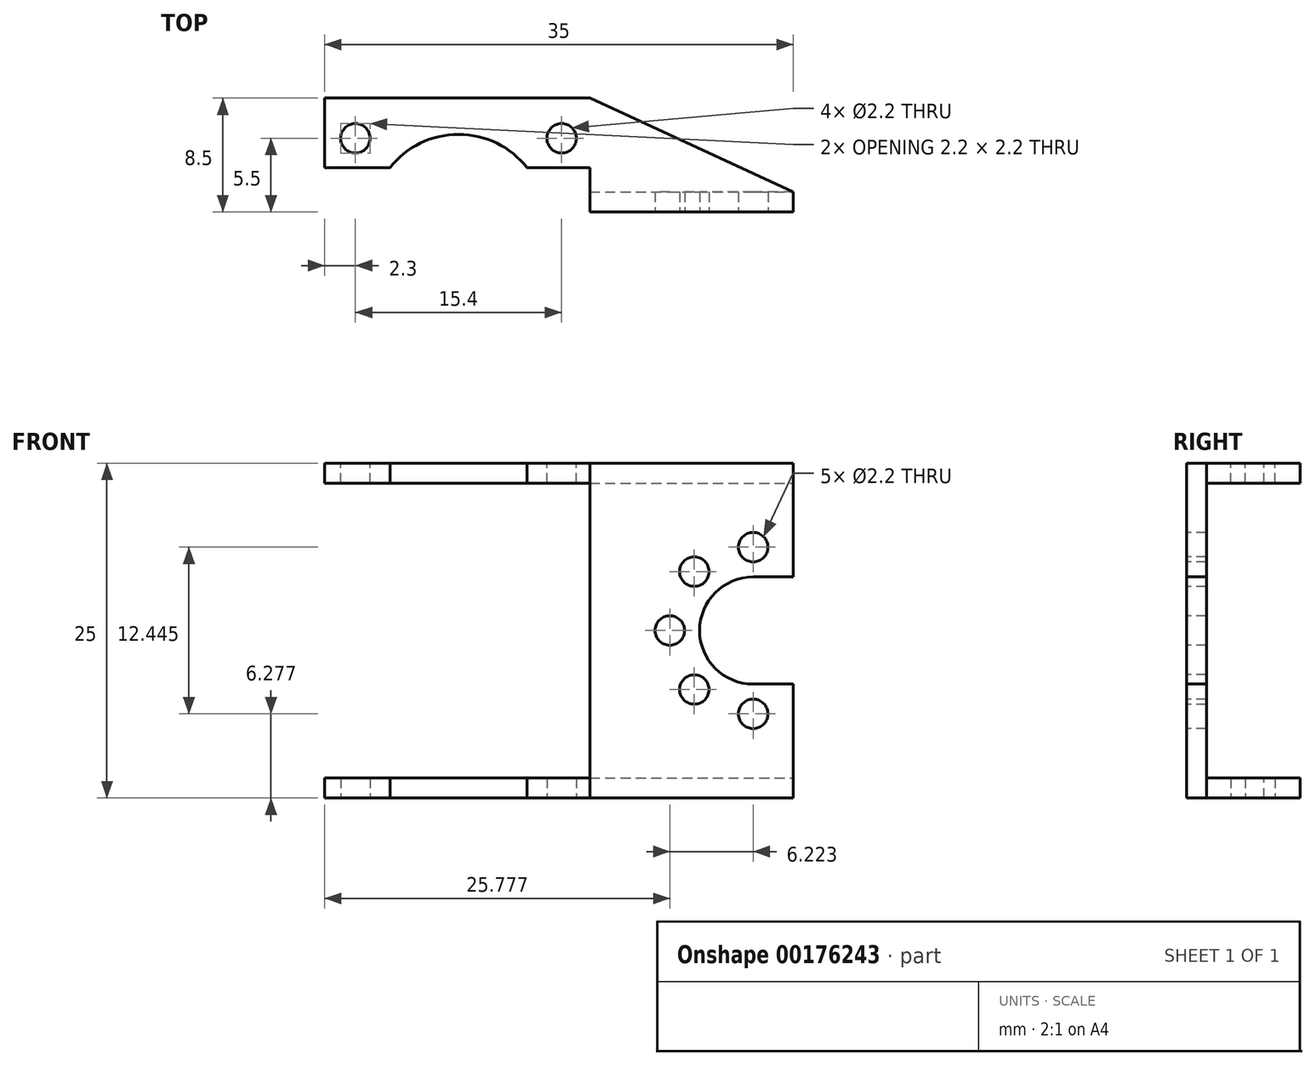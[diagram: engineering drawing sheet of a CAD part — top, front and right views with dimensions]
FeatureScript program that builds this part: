
annotation { "Feature Type Name" : "Feature", "Feature Type Description" : "" }
export const myFeature = defineFeature(function(context is Context, id is Id, definition is map)
    precondition{}
    {
        {
            var Q0;
            Q0=qCreatedBy(makeId("Top.planeOp"),FACE);
            var sketch = newSketch(context, id + "F0", { "sketchPlane" : qUnion([Q0])});
            skLineSegment(sketch, "E0.bottom", {"start": v(-10, 0.75) * mm, "end": v(10, 0.75) * mm});
            skLineSegment(sketch, "E0.top", {"start": v(-10, -0.75) * mm, "end": v(10, -0.75) * mm});
            skLineSegment(sketch, "E0.left", {"start": v(-10, 0.75) * mm, "end": v(-10, -0.75) * mm});
            skLineSegment(sketch, "E0.right", {"start": v(10, 0.75) * mm, "end": v(10, -0.75) * mm});
            skPoint(sketch, "E0.middle", {"position": v(0, 0) * mm});
            skSolve(sketch);
        }
        {
            var Q0;
            Q0=qSketchRegion(id+"F0",true);
            extrude(context, id + "F1", {"entities" : qUnion([Q0]), "depth" : (11 + 1.5) * mm});
        }
        {
            var Q0;
            Q0=makeQuery(id+"F1.opExtrude","SWEPT_FACE",FACE,{"disambiguationData":[OSD([sQuery(id+"F0.wireOp",EDGE,"E0.bottom")])]});
            var sketch = newSketch(context, id + "F2", { "sketchPlane" : qUnion([Q0])});
            skLineSegment(sketch, "E1.bottom", {"start": v(10, 12.5) * mm, "end": v(-10, 12.5) * mm});
            skLineSegment(sketch, "E1.top", {"start": v(10, 11) * mm, "end": v(-10, 11) * mm});
            skLineSegment(sketch, "E1.left", {"start": v(10, 12.5) * mm, "end": v(10, 11) * mm});
            skLineSegment(sketch, "E1.right", {"start": v(-10, 12.5) * mm, "end": v(-10, 11) * mm});
            skSolve(sketch);
        }
        {
            var Q0;
            Q0=qSketchRegion(id+"F2",true);
            extrude(context, id + "F3", {"entities" : qUnion([Q0]), "operationType" : NewBodyOperationType.ADD, "depth" : (10 - 1.5) * mm});
        }
        {
            var Q0;
            Q0=makeQuery(id+"F3.boolean.opBoolean","MERGE",FACE,{"derivedFrom":[makeQuery(id+"F1.opExtrude","CAP_FACE",FACE,{"disambiguationData":[OSD([sQuery(id+"F0.wireOp",EDGE,"E0.bottom"),sQuery(id+"F0.wireOp",EDGE,"E0.top"),sQuery(id+"F0.wireOp",EDGE,"E0.left"),sQuery(id+"F0.wireOp",EDGE,"E0.right")])],"isStart":false}),makeQuery(id+"F3.opExtrude","SWEPT_FACE",FACE,{"disambiguationData":[OSD([sQuery(id+"F2.wireOp",EDGE,"E1.bottom")])]})]});
            var sketch = newSketch(context, id + "F4", { "sketchPlane" : qUnion([Q0])});
            skLineSegment(sketch, "E2", {"start": v(-10, 4.75) * mm, "end": v(10, 4.75) * mm, "construction": true});
            skCircle(sketch, "E3", {"center": v(-7.7, 4.75) * mm, "radius": 1.1 * mm});
            skCircle(sketch, "E4.MirrorC", {"center": v(7.7, 4.75) * mm, "radius": 1.1 * mm});
            skSolve(sketch);
        }
        {
            var Q0;
            Q0=qSketchRegion(id+"F4",true);
            extrude(context, id + "F5", {"entities" : qUnion([Q0]), "operationType" : NewBodyOperationType.REMOVE, "endBound" : BoundingType.UP_TO_NEXT, "oppositeDirection" : true, "depth" : 25 * mm});
        }
        {
            var Q0;
            Q0=makeQuery(id+"F1.opExtrude","SWEPT_BODY",BODY,{"disambiguationData":[OSD([sQuery(id+"F0.wireOp",EDGE,"E0.bottom"),sQuery(id+"F0.wireOp",EDGE,"E0.top"),sQuery(id+"F0.wireOp",EDGE,"E0.left"),sQuery(id+"F0.wireOp",EDGE,"E0.right")])]});
            var Q1;
            Q1=qCreatedBy(makeId("Top.planeOp"),FACE);
            mirror(context, id + "F6", {"operationType" : NewBodyOperationType.ADD, "entities" : qUnion([Q0]), "mirrorPlane" : qUnion([Q1])});
        }
        {
            var Q0;
            {var subQ0=makeQuery(id+"F3.boolean.opBoolean","MERGE",FACE,{"derivedFrom":[makeQuery(id+"F1.opExtrude","SWEPT_FACE",FACE,{"disambiguationData":[OSD([sQuery(id+"F0.wireOp",EDGE,"E0.right")])]}),makeQuery(id+"F3.opExtrude","SWEPT_FACE",FACE,{"disambiguationData":[OSD([sQuery(id+"F2.wireOp",EDGE,"E1.right")])]})]});Q0=makeQuery(id+"F6.boolean.opBoolean","MERGE",FACE,{"derivedFrom":[subQ0,makeQuery(id+"F6.opPattern","COPY",FACE,{"derivedFrom":subQ0,"instanceName":"1"})]});}
            var sketch = newSketch(context, id + "F7", { "sketchPlane" : qUnion([Q0])});
            skLineSegment(sketch, "E5.0", {"start": v(9.25, -12.5) * mm, "end": v(-0.75, -12.5) * mm});
            skLineSegment(sketch, "E5.1", {"start": v(9.25, 11) * mm, "end": v(0.75, 11) * mm});
            skLineSegment(sketch, "E5.2", {"start": v(9.25, -11) * mm, "end": v(0.75, -11) * mm});
            skLineSegment(sketch, "E5.3", {"start": v(9.25, 12.5) * mm, "end": v(-0.75, 12.5) * mm});
            skLineSegment(sketch, "E5.4", {"start": v(9.25, 11) * mm, "end": v(0.75, 11) * mm});
            skLineSegment(sketch, "E5.5", {"start": v(5.85, 12.5) * mm, "end": v(3.65, 12.5) * mm});
            skLineSegment(sketch, "E5.7", {"start": v(9.25, -12.5) * mm, "end": v(-0.75, -12.5) * mm});
            skLineSegment(sketch, "E5.8", {"start": v(9.25, -12.5) * mm, "end": v(9.25, -11) * mm});
            skLineSegment(sketch, "E5.9", {"start": v(9.25, 12.5) * mm, "end": v(9.25, 11) * mm});
            skLineSegment(sketch, "E5.10", {"start": v(9.25, 12.5) * mm, "end": v(-0.75, 12.5) * mm});
            skLineSegment(sketch, "E5.13", {"start": v(9.25, -11) * mm, "end": v(0.75, -11) * mm});
            skLineSegment(sketch, "E5.14", {"start": v(0.75, 11) * mm, "end": v(0.75, -11) * mm});
            skLineSegment(sketch, "E5.15", {"start": v(-0.75, 12.5) * mm, "end": v(-0.75, -12.5) * mm});
            skLineSegment(sketch, "E5.16", {"start": v(5.85, -11) * mm, "end": v(3.65, -11) * mm});
            skLineSegment(sketch, "E5.20", {"start": v(5.85, 11) * mm, "end": v(3.65, 11) * mm});
            skLineSegment(sketch, "E5.21", {"start": v(3.65, -11) * mm, "end": v(5.85, -11) * mm});
            skLineSegment(sketch, "E5.22", {"start": v(-0.75, 12.5) * mm, "end": v(-0.75, -12.5) * mm});
            skLineSegment(sketch, "E5.23", {"start": v(5.85, -12.5) * mm, "end": v(3.65, -12.5) * mm});
            skLineSegment(sketch, "E5.24", {"start": v(0.75, 11) * mm, "end": v(0.75, -11) * mm});
            skLineSegment(sketch, "E5.26", {"start": v(3.65, 12.5) * mm, "end": v(5.85, 12.5) * mm});
            skLineSegment(sketch, "E5.28", {"start": v(9.25, -12.5) * mm, "end": v(9.25, -11) * mm});
            skLineSegment(sketch, "E5.29", {"start": v(3.65, -12.5) * mm, "end": v(5.85, -12.5) * mm});
            skLineSegment(sketch, "E5.30", {"start": v(9.25, 12.5) * mm, "end": v(9.25, 11) * mm});
            skLineSegment(sketch, "E5.31", {"start": v(3.65, 11) * mm, "end": v(5.85, 11) * mm});
            skSolve(sketch);
        }
        {
            var Q0;
            Q0=qSketchRegion(id+"F7",true);
            extrude(context, id + "F8", {"entities" : qUnion([Q0]), "operationType" : NewBodyOperationType.ADD, "depth" : 15 * mm});
        }
        {
            var Q0;
            {var subQ0=makeQuery(id+"F1.opExtrude","SWEPT_FACE",FACE,{"disambiguationData":[OSD([sQuery(id+"F0.wireOp",EDGE,"E0.top")])]});Q0=makeQuery(id+"F8.boolean.opBoolean","MERGE",FACE,{"derivedFrom":[makeQuery(id+"F6.boolean.opBoolean","MERGE",FACE,{"derivedFrom":[subQ0,makeQuery(id+"F6.opPattern","COPY",FACE,{"derivedFrom":subQ0,"instanceName":"1"})]}),makeQuery(id+"F8.opExtrude","SWEPT_FACE",FACE,{"disambiguationData":[OSD([sQuery(id+"F7.wireOp",EDGE,"E5.22")])]})]});}
            var sketch = newSketch(context, id + "F9", { "sketchPlane" : qUnion([Q0])});
            skArc(sketch, "E6", {"start": v(22, 4) * mm, "mid": v(18, 0) * mm, "end": v(22, -4) * mm});
            skLineSegment(sketch, "E7.bottom", {"start": v(17.6, -4.4) * mm, "end": v(26.4, -4.4) * mm, "construction": true});
            skLineSegment(sketch, "E7.top", {"start": v(17.6, 4.4) * mm, "end": v(26.4, 4.4) * mm, "construction": true});
            skLineSegment(sketch, "E7.left", {"start": v(17.6, -4.4) * mm, "end": v(17.6, 4.4) * mm, "construction": true});
            skLineSegment(sketch, "E7.right", {"start": v(26.4, -4.4) * mm, "end": v(26.4, 4.4) * mm, "construction": true});
            skCircle(sketch, "E8", {"center": v(17.6, -4.4) * mm, "radius": 1.1 * mm});
            skCircle(sketch, "E9.1.0", {"center": v(22, -6.22) * mm, "radius": 1.1 * mm});
            skCircle(sketch, "E9.5.0", {"center": v(22, 6.22) * mm, "radius": 1.1 * mm});
            skCircle(sketch, "E9.6.0", {"center": v(17.6, 4.4) * mm, "radius": 1.1 * mm});
            skCircle(sketch, "E9.7.0", {"center": v(15.78, 0) * mm, "radius": 1.1 * mm});
            skLineSegment(sketch, "E10", {"start": v(22, -4) * mm, "end": v(25, -4) * mm});
            skLineSegment(sketch, "E11", {"start": v(22, 4) * mm, "end": v(25, 4) * mm});
            skLineSegment(sketch, "E12", {"start": v(25, -4) * mm, "end": v(25, 4) * mm});
            skLineSegment(sketch, "E13.bottom", {"start": v(-10, -12.5) * mm, "end": v(9.8, -12.5) * mm});
            skLineSegment(sketch, "E13.top", {"start": v(-10, 12.5) * mm, "end": v(9.8, 12.5) * mm});
            skLineSegment(sketch, "E13.left", {"start": v(-10, -12.5) * mm, "end": v(-10, 12.5) * mm});
            skLineSegment(sketch, "E13.right", {"start": v(9.8, -12.5) * mm, "end": v(9.8, 12.5) * mm});
            skSolve(sketch);
        }
        {
            var Q0;
            Q0=qSketchRegion(id+"F9",true);
            extrude(context, id + "F10", {"entities" : qUnion([Q0]), "operationType" : NewBodyOperationType.REMOVE, "oppositeDirection" : true, "depth" : 3.3 * mm});
        }
        {
            var Q0;
            Q0=makeQuery(id+"F8.boolean.opBoolean","MERGE",FACE,{"derivedFrom":[makeQuery(id+"F3.boolean.opBoolean","MERGE",FACE,{"derivedFrom":[makeQuery(id+"F1.opExtrude","CAP_FACE",FACE,{"disambiguationData":[OSD([sQuery(id+"F0.wireOp",EDGE,"E0.bottom"),sQuery(id+"F0.wireOp",EDGE,"E0.top"),sQuery(id+"F0.wireOp",EDGE,"E0.left"),sQuery(id+"F0.wireOp",EDGE,"E0.right")])],"isStart":false}),makeQuery(id+"F3.opExtrude","SWEPT_FACE",FACE,{"disambiguationData":[OSD([sQuery(id+"F2.wireOp",EDGE,"E1.bottom")])]})]}),makeQuery(id+"F8.opExtrude","SWEPT_FACE",FACE,{"disambiguationData":[OSD([sQuery(id+"F7.wireOp",EDGE,"E5.10"),sQuery(id+"F7.wireOp",EDGE,"E5.26")])]})]});
            var sketch = newSketch(context, id + "F11", { "sketchPlane" : qUnion([Q0])});
            skArc(sketch, "E14", {"start": v(5.12, 2.55) * mm, "mid": v(0, 5.05) * mm, "end": v(-5.12, 2.55) * mm});
            skPoint(sketch, "E15", {"position": v(-7.7, 4.75) * mm});
            skPoint(sketch, "E16", {"position": v(7.7, 4.75) * mm});
            skLineSegment(sketch, "E17", {"start": v(-7.7, 4.75) * mm, "end": v(7.7, 4.75) * mm, "construction": true});
            skPoint(sketch, "E18", {"position": v(0, 4.75) * mm});
            skLineSegment(sketch, "E19", {"start": v(-5.12, 2.55) * mm, "end": v(5.12, 2.55) * mm});
            skLineSegment(sketch, "E20", {"start": v(-10, 7.75) * mm, "end": v(9.8, 7.75) * mm});
            skLineSegment(sketch, "E21", {"start": v(9.8, 7.75) * mm, "end": v(25, 0.75) * mm});
            skLineSegment(sketch, "E22", {"start": v(-10, 7.55) * mm, "end": v(9.8, 7.55) * mm, "construction": true});
            skLineSegment(sketch, "E23", {"start": v(9.8, 7.75) * mm, "end": v(9.8, 7.55) * mm, "construction": true});
            skSolve(sketch);
        }
        {
            var Q0;
            Q0=qSketchRegion(id+"F11",true);
            var Q1;
            {var subQ5=sQuery(id+"F11.wireOp",EDGE,"E20");Q1=makeQuery(id+"F11.imprint","IMPRINT",FACE,{"disambiguationData":[TD([[makeQuery(id+"F11.imprint","IMPRINT",EDGE,{"derivedFrom":subQ5}),1.0]])]});}
            var Q2;
            {var subQ4=sQuery(id+"F11.wireOp",EDGE,"E21");Q2=makeQuery(id+"F11.imprint","IMPRINT",FACE,{"disambiguationData":[TD([[makeQuery(id+"F11.imprint","IMPRINT",EDGE,{"derivedFrom":subQ4}),1.0]])]});}
            extrude(context, id + "F12", {"entities" : qUnion([Q0, Q1, Q2]), "operationType" : NewBodyOperationType.REMOVE, "endBound" : BoundingType.THROUGH_ALL, "oppositeDirection" : true, "depth" : 25 * mm});
        }
    });
